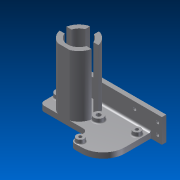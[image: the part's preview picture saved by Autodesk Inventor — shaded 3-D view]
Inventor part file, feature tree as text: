
AUTODESK INVENTOR PART (.ipt)
format: ipt  version: 2012 (Build 160160000, 160)  size: 206,848 bytes
history: native  units: in
note: dims shown in document units (in); Inventor stores cm internally (conversion verified against a paired STEP export)
features: fillet x1, other x1, imported_body x1
ambient origin geometry x8: Origin, YZ Plane, XZ Plane, XY Plane, X Axis, Y Axis, Z Axis, Center Point
feature tree (3):
  fillet  "Redondeo4"  [1 undecoded]
  other  "Despliegue31"
  imported_body  "Base1"
note: 1 required parameter value undecoded (feature->parameter linkage not recoverable at this tier; creation-order binding heuristic only, values carry confidence <= 0.55)
